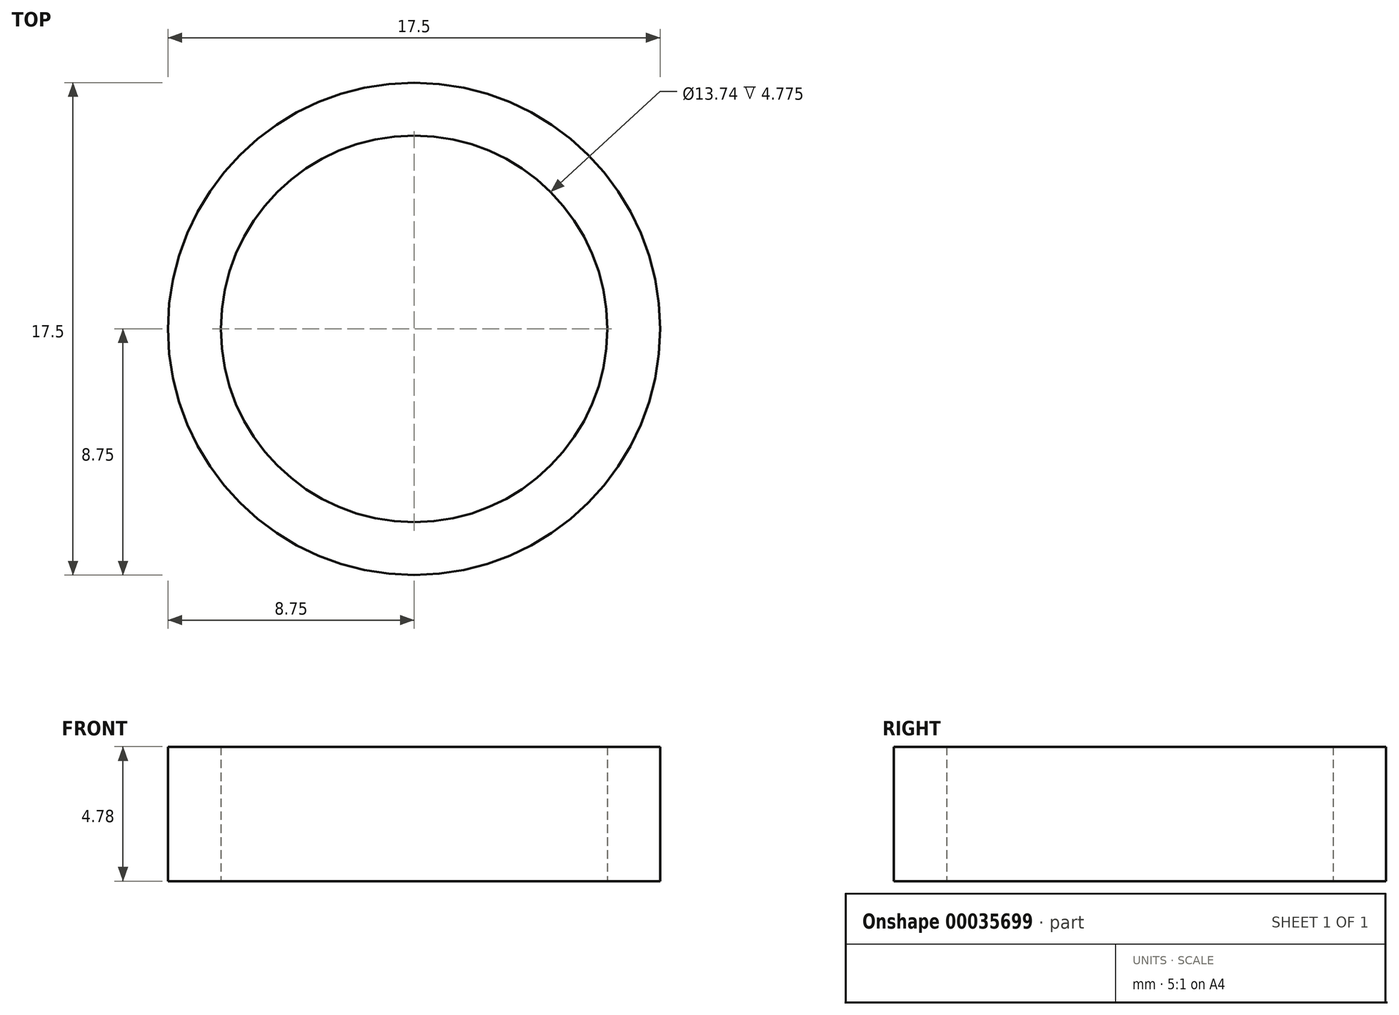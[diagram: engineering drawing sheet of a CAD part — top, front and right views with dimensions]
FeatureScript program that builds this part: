
annotation { "Feature Type Name" : "Feature", "Feature Type Description" : "" }
export const myFeature = defineFeature(function(context is Context, id is Id, definition is map)
    precondition{}
    {
        {
            var Q0;
            Q0=qCreatedBy(makeId("Front.planeOp"),FACE);
            var sketch = newSketch(context, id + "F0", { "sketchPlane" : qUnion([Q0])});
            skLineSegment(sketch, "E0", {"start": v(0, 0) * mm, "end": v(0, 4.78) * mm});
            skLineSegment(sketch, "E1", {"start": v(0, 4.78) * mm, "end": v(6.87, 4.78) * mm});
            skLineSegment(sketch, "E2", {"start": v(6.87, 4.78) * mm, "end": v(6.87, 0) * mm});
            skLineSegment(sketch, "E3", {"start": v(6.87, 0) * mm, "end": v(0, 0) * mm});
            skLineSegment(sketch, "E4", {"start": v(6.87, 4.78) * mm, "end": v(8.75, 4.78) * mm});
            skLineSegment(sketch, "E5", {"start": v(8.75, 4.78) * mm, "end": v(8.75, 0) * mm});
            skLineSegment(sketch, "E6", {"start": v(8.75, 0) * mm, "end": v(6.87, 0) * mm});
            skSolve(sketch);
        }
        {
            var Q0;
            Q0=makeQuery(id+"F0.imprint","IMPRINT",FACE,{"disambiguationData":[TD([[makeQuery(id+"F0.imprint","IMPRINT",EDGE,{"derivedFrom":sQuery(id+"F0.wireOp",EDGE,"E2")}),1.0]])]});
            var Q1;
            Q1=sQuery(id+"F0.wireOp",EDGE,"E0");
            revolve(context, id + "F1", {"entities" : qUnion([Q0]), "axis" : qUnion([Q1]), "revolveType" : RevolveType.FULL});
        }
    });
